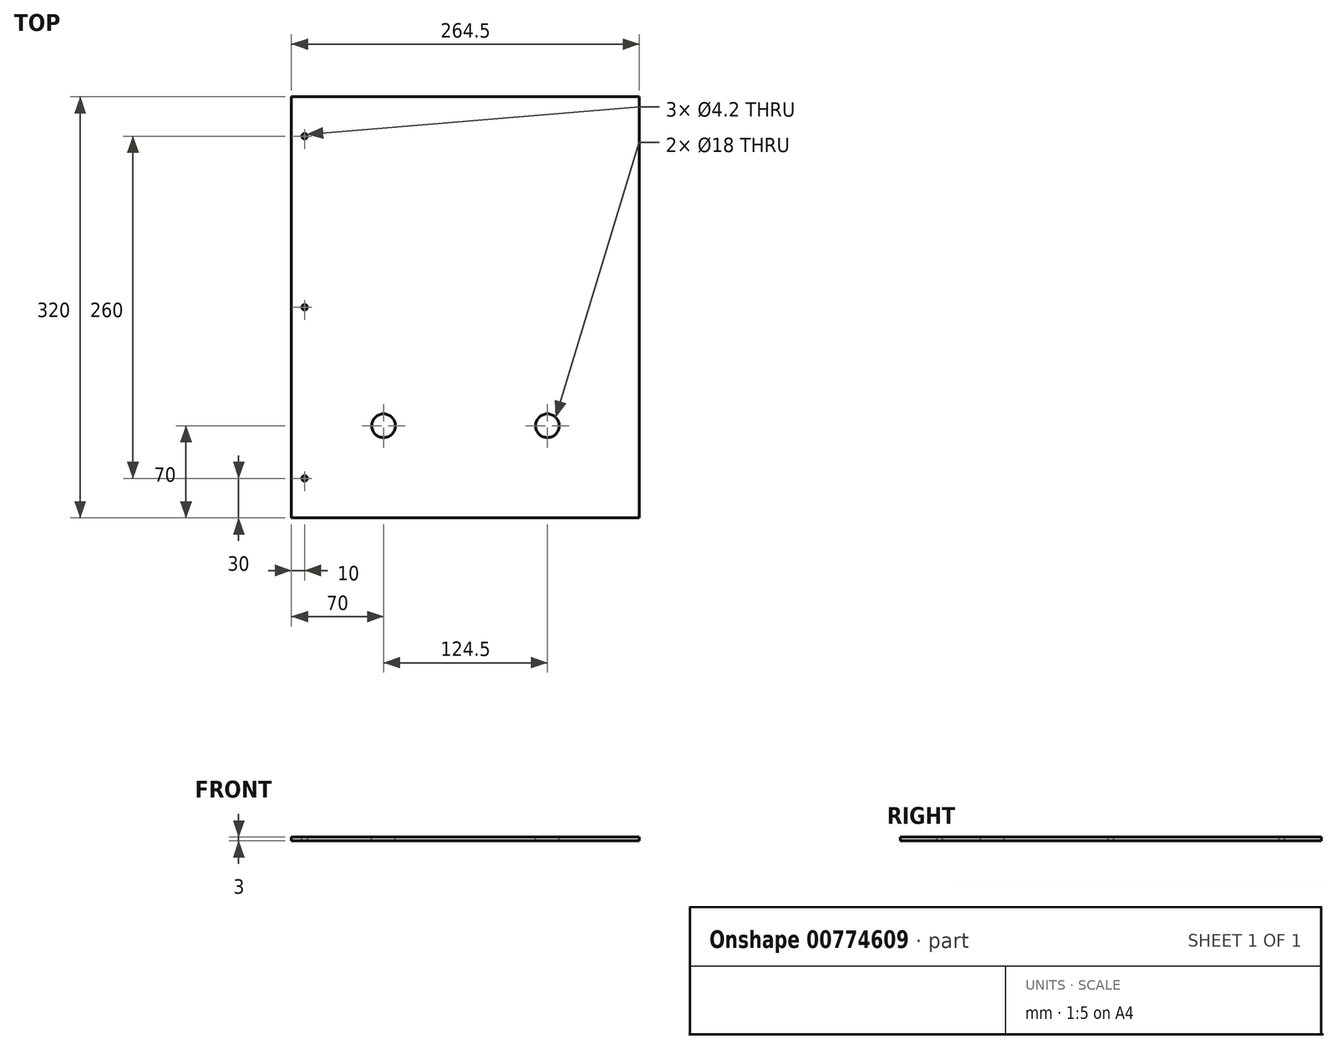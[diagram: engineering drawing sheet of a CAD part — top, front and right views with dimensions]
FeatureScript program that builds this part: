
annotation { "Feature Type Name" : "Feature", "Feature Type Description" : "" }
export const myFeature = defineFeature(function(context is Context, id is Id, definition is map)
    precondition{}
    {
        {
            assignVariable(context, id + "F0", {"name" : "Epaisseur", "anyValue" : 3});
        }
        {
            var Q0;
            Q0=qCreatedBy(makeId("Top.planeOp"),FACE);
            var sketch = newSketch(context, id + "F1", { "sketchPlane" : qUnion([Q0])});
            skLineSegment(sketch, "E0.bottom", {"start": v(-132.25, -160) * mm, "end": v(132.25, -160) * mm});
            skLineSegment(sketch, "E0.top", {"start": v(-132.25, 160) * mm, "end": v(132.25, 160) * mm});
            skLineSegment(sketch, "E0.left", {"start": v(-132.25, -160) * mm, "end": v(-132.25, 160) * mm});
            skLineSegment(sketch, "E0.right", {"start": v(132.25, -160) * mm, "end": v(132.25, 160) * mm});
            skPoint(sketch, "E0.middle", {"position": v(0, 0) * mm});
            skSolve(sketch);
        }
        {
            var Q0;
            Q0=makeQuery(id+"F1.imprint","IMPRINT",FACE,{"disambiguationData":[TD([[makeQuery(id+"F1.imprint","IMPRINT",EDGE,{"derivedFrom":sQuery(id+"F1.wireOp",EDGE,"E0.bottom")}),1.0]])]});
            extrude(context, id + "F2", {"entities" : qUnion([Q0]), "depth" : (getVariable(context, 'Epaisseur')) * mm, "offsetDistance" : 25 * mm});
        }
        {
            var Q0;
            Q0=makeQuery(id+"F2.opExtrude","CAP_FACE",FACE,{"disambiguationData":[OSD([sQuery(id+"F1.wireOp",EDGE,"E0.bottom"),sQuery(id+"F1.wireOp",EDGE,"E0.top"),sQuery(id+"F1.wireOp",EDGE,"E0.left"),sQuery(id+"F1.wireOp",EDGE,"E0.right")])],"isStart":false});
            var sketch = newSketch(context, id + "F3", { "sketchPlane" : qUnion([Q0])});
            skLineSegment(sketch, "E1", {"start": v(-122.25, 160) * mm, "end": v(-122.25, -160) * mm, "construction": true});
            skPoint(sketch, "E2", {"position": v(-122.25, 130) * mm});
            skPoint(sketch, "E3", {"position": v(-122.25, 0) * mm});
            skPoint(sketch, "E4", {"position": v(-122.25, -130) * mm});
            skSolve(sketch);
        }
        {
            var Q0;
            Q0=sQuery(id+"F3.wireOp",VERTEX,"E2");
            var Q1;
            Q1=sQuery(id+"F3.wireOp",VERTEX,"E3");
            var Q2;
            Q2=sQuery(id+"F3.wireOp",VERTEX,"E4");
            var Q3;
            Q3=makeQuery(id+"F2.opExtrude","SWEPT_BODY",BODY,{"disambiguationData":[OSD([sQuery(id+"F1.wireOp",EDGE,"E0.bottom"),sQuery(id+"F1.wireOp",EDGE,"E0.top"),sQuery(id+"F1.wireOp",EDGE,"E0.left"),sQuery(id+"F1.wireOp",EDGE,"E0.right")])]});
            hole(context, id + "F4", {"style" : HoleStyle.SIMPLE, "endStyle" : HoleEndStyle.BLIND, "holeDiameter" : 4.2 * mm, "majorDiameter" : 5 * mm, "holeDepth" : 4 * mm, "isTappedThrough" : true, "tappedDepth" : 2.3 * mm, "tapClearance" : 3, "startFromSketch" : true, "locations" : qUnion([Q0, Q1, Q2]), "scope" : qUnion([Q3])});
        }
        {
            var Q0;
            Q0=makeQuery(id+"F2.opExtrude","CAP_FACE",FACE,{"disambiguationData":[OSD([sQuery(id+"F1.wireOp",EDGE,"E0.bottom"),sQuery(id+"F1.wireOp",EDGE,"E0.top"),sQuery(id+"F1.wireOp",EDGE,"E0.left"),sQuery(id+"F1.wireOp",EDGE,"E0.right")])],"isStart":false});
            var sketch = newSketch(context, id + "F5", { "sketchPlane" : qUnion([Q0])});
            skCircle(sketch, "E5", {"center": v(-62.25, -90) * mm, "radius": 9 * mm});
            skCircle(sketch, "E6", {"center": v(62.25, -90) * mm, "radius": 9 * mm});
            skSolve(sketch);
        }
        {
            var Q0;
            Q0 = qSketchRegion(id + "F5", true);
            extrude(context, id + "F6", {"entities" : qUnion([Q0]), "operationType" : NewBodyOperationType.REMOVE, "endBound" : BoundingType.UP_TO_NEXT, "oppositeDirection" : true, "depth" : 25 * mm, "offsetDistance" : 25 * mm});
        }
    });
